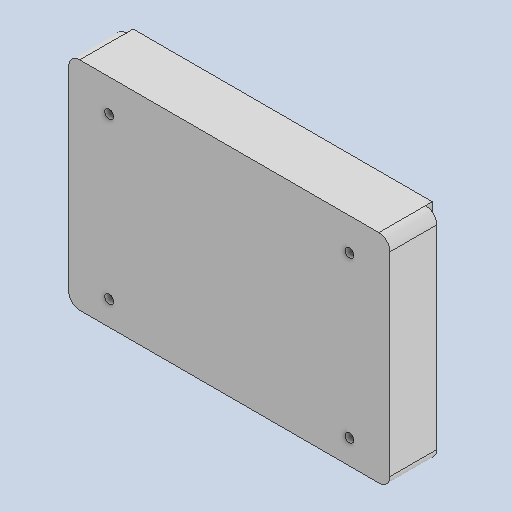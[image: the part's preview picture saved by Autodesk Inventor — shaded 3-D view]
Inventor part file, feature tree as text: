
AUTODESK INVENTOR PART (.ipt)
format: ipt  version: 2024.2 (Build 282272000, 272)  size: 160,256 bytes
history: native  units: mm
features: extrude x3, fillet x1, sketch x1
ambient origin geometry x8: Origin, YZ Plane, XZ Plane, XY Plane, X Axis, Y Axis, Z Axis, Center Point
bodies: Solid1 (feature_tree)
feature tree (5):
  extrude  "Extrusion1"  Depth=39.0mm
  extrude  "Extrusion2"  Depth=9.61mm TaperAngle=0.0deg
  extrude  "Extrusion3"  Depth=2.0mm
  fillet  "Fillet1"  Radius=4.4mm
  sketch  "Sketch2"  dims[d0=57.8mm d1=39.0mm d2=9.61mm d3=0.0mm d4=1.6mm d5=4.4mm d6=7.3mm d7=5.8mm d8=0.0mm d9=0.0mm d10=6.2mm d11=21.9mm d12=11.05mm d13=2.0mm d14=2.0mm d15=1.2mm d16=0.0mm d17=2.0mm]
